# Revit family: NLRS_74_PF_UN_toilet_S8002300000_SPHINX_BCB
name_source: partatom
category: Plumbing Fixtures
revit_build: Autodesk Revit 2016 (Build: 20150220_1215(x64)
units: mm (PartAtom-declared; Revit-internal decimal feet)

## family parameters
Always vertical = Yes
Cut with Voids When Loaded = No
OmniClass Number = 23.45.00.00
OmniClass Title = Sanitary, Laundry, and Cleaning Equipment
Part Type = Normal
Room Calculation Point = No
Round Connector Dimension = Use Radius
Shared = No
Work Plane-Based = No

## types (1)
- kindercloset 14 PK
    Assembly Code = 4(74.11)
    CWFU = 0
    Description = toilet
    IfcElement = IfcFlowTerminal
    IfcExportAs = IfcSanitaryTerminalTypeEnum
    IfcExportType = TOILETPAN
    IfcTypeProduct = IfcSanitaryTerminalType
    Keynote = kindercloset
    Manufacturer = Sphinx
    Model = 300 kindercloset 14 PK
    NLRS_C_URL_BCB = http://bcb-online.nl
    NLRS_C_URL_product_data = http://www.sphinx.nl
    NLRS_C_breedte = 350 mm  [stored 1.14829 ft]
    NLRS_C_code_EAN = 8711754391321
    NLRS_C_code_artikel = S8002300000
    NLRS_C_content_datum_gewijzigd = APR-2018
    NLRS_C_content_datum_uitgifte = APR-2018
    NLRS_C_content_provider = BouwConnect
    NLRS_C_content_versie = 2.0
    NLRS_C_diameter_in = 55 mm  [stored 0.180446 ft]
    NLRS_C_diameter_uit = 102 mm
    NLRS_C_hoogte = 340 mm  [stored 1.11549 ft]
    NLRS_C_lengte = 500 mm  [stored 1.64042 ft]
    NLRS_C_materiaal = NLRS_g3_porcelein_wit
    NLRS_C_revit_versie = 2016
    NLRS_C_serie = Sphinx 300 Kids
    NLRS_C_type = Staand closet diepspoel
    NLRS_S_gewicht = 14.00 kg
    URL = http://www.sphinx.nl
    WFU = 0
    Waste Connection = Yes

note: [stored X ft] marks values corroborated as IEEE doubles in the binary element streams (Revit-internal decimal feet)

## geometry (parser evidence)
native form markers: Blend x790, Sweep x2
no freeform markers — native parametric forms only
